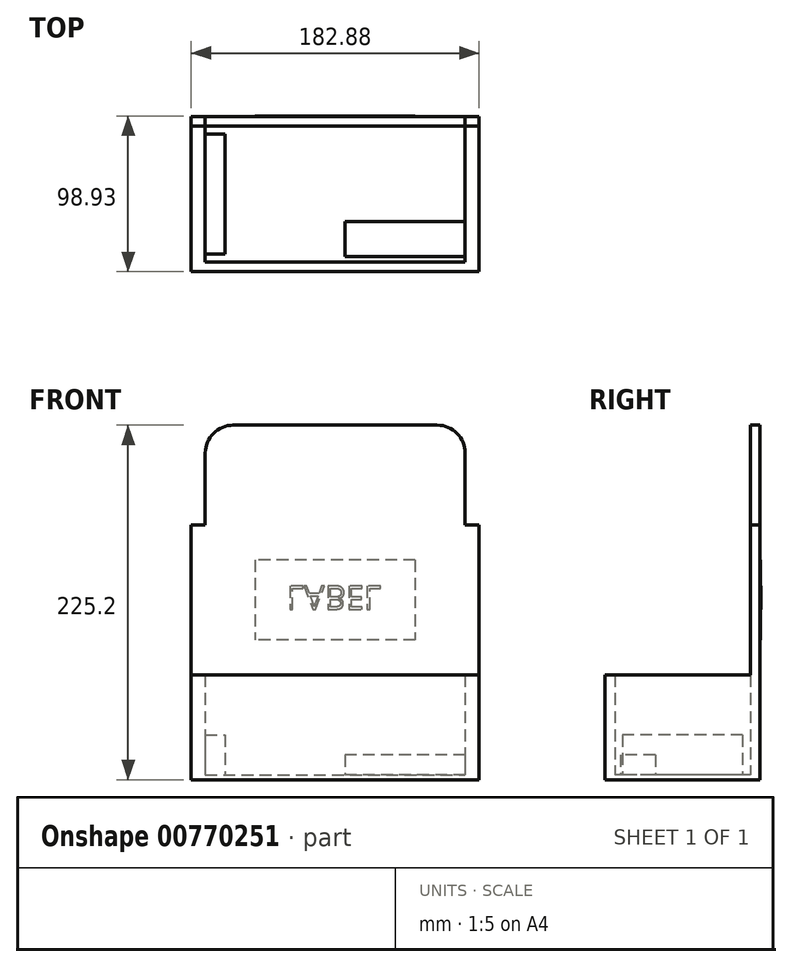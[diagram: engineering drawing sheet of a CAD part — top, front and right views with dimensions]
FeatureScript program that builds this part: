
annotation { "Feature Type Name" : "Feature", "Feature Type Description" : "" }
export const myFeature = defineFeature(function(context is Context, id is Id, definition is map)
    precondition{}
    {
        {
            var Q0;
            Q0=qCreatedBy(makeId("Top.planeOp"),FACE);
            var sketch = newSketch(context, id + "F0", { "sketchPlane" : qUnion([Q0])});
            skLineSegment(sketch, "E0.bottom", {"start": v(91.44, 49.21) * mm, "end": v(-91.44, 49.21) * mm});
            skLineSegment(sketch, "E0.top", {"start": v(91.44, -49.21) * mm, "end": v(-91.44, -49.21) * mm});
            skLineSegment(sketch, "E0.left", {"start": v(91.44, 49.21) * mm, "end": v(91.44, -49.21) * mm});
            skLineSegment(sketch, "E0.right", {"start": v(-91.44, 49.21) * mm, "end": v(-91.44, -49.21) * mm});
            skPoint(sketch, "E0.middle", {"position": v(0, 0) * mm});
            skSolve(sketch);
        }
        {
            var Q0;
            Q0=makeQuery(id+"F0.imprint","IMPRINT",FACE,{"disambiguationData":[TD([[makeQuery(id+"F0.imprint","IMPRINT",EDGE,{"derivedFrom":sQuery(id+"F0.wireOp",EDGE,"E0.bottom")}),1.0]])]});
            extrude(context, id + "F1", {"entities" : qUnion([Q0]), "depth" : 2.95 * mm});
        }
        {
            var Q0;
            Q0=makeQuery(id+"F1.opExtrude","CAP_FACE",FACE,{"disambiguationData":[OSD([sQuery(id+"F0.wireOp",EDGE,"E0.bottom"),sQuery(id+"F0.wireOp",EDGE,"E0.top"),sQuery(id+"F0.wireOp",EDGE,"E0.left"),sQuery(id+"F0.wireOp",EDGE,"E0.right")])],"isStart":false});
            var sketch = newSketch(context, id + "F2", { "sketchPlane" : qUnion([Q0])});
            skLineSegment(sketch, "E1.bottom", {"start": v(-91.44, 49.21) * mm, "end": v(-82.55, 49.21) * mm});
            skLineSegment(sketch, "E1.top", {"start": v(-91.44, -49.21) * mm, "end": v(-82.55, -49.21) * mm});
            skLineSegment(sketch, "E1.left", {"start": v(-91.44, 49.21) * mm, "end": v(-91.44, -49.21) * mm});
            skLineSegment(sketch, "E1.right", {"start": v(-82.55, 49.21) * mm, "end": v(-82.55, -49.21) * mm});
            skLineSegment(sketch, "E2.MirrorCS", {"start": v(82.55, 49.21) * mm, "end": v(82.55, -49.21) * mm});
            skLineSegment(sketch, "E3.MirrorCS", {"start": v(91.44, 49.21) * mm, "end": v(82.55, 49.21) * mm});
            skLineSegment(sketch, "E4.MirrorCS", {"start": v(91.44, -49.21) * mm, "end": v(82.55, -49.21) * mm});
            skLineSegment(sketch, "E5.MirrorCS", {"start": v(91.44, 49.21) * mm, "end": v(91.44, -49.21) * mm});
            skLineSegment(sketch, "E6", {"start": v(-82.55, -49.21) * mm, "end": v(-82.55, -43.1) * mm});
            skLineSegment(sketch, "E7", {"start": v(-82.55, -43.1) * mm, "end": v(82.55, -43.1) * mm});
            skLineSegment(sketch, "E8", {"start": v(-82.55, -49.21) * mm, "end": v(82.55, -49.21) * mm});
            skLineSegment(sketch, "E9.MirrorCS", {"start": v(-82.55, 43.1) * mm, "end": v(82.55, 43.1) * mm});
            skLineSegment(sketch, "E10.MirrorCS", {"start": v(-82.55, 49.21) * mm, "end": v(82.55, 49.21) * mm});
            skSolve(sketch);
        }
        {
            var Q0;
            Q0=qSketchRegion(id+"F2",true);
            extrude(context, id + "F3", {"entities" : qUnion([Q0]), "operationType" : NewBodyOperationType.ADD, "depth" : 63.5 * mm});
        }
        {
            var Q0;
            Q0=makeQuery(id+"F3.opExtrude","CAP_FACE",FACE,{"disambiguationData":[OSD([sQuery(id+"F2.wireOp",EDGE,"E1.bottom"),sQuery(id+"F2.wireOp",EDGE,"E1.top"),sQuery(id+"F2.wireOp",EDGE,"E1.left"),sQuery(id+"F2.wireOp",EDGE,"E1.right"),sQuery(id+"F2.wireOp",EDGE,"E2.MirrorCS"),sQuery(id+"F2.wireOp",EDGE,"E3.MirrorCS"),sQuery(id+"F2.wireOp",EDGE,"E4.MirrorCS"),sQuery(id+"F2.wireOp",EDGE,"E5.MirrorCS"),sQuery(id+"F2.wireOp",EDGE,"E7"),sQuery(id+"F2.wireOp",EDGE,"E8"),sQuery(id+"F2.wireOp",EDGE,"E9.MirrorCS"),sQuery(id+"F2.wireOp",EDGE,"E10.MirrorCS")])],"isStart":false});
            var sketch = newSketch(context, id + "F4", { "sketchPlane" : qUnion([Q0])});
            skLineSegment(sketch, "E11.bottom", {"start": v(-91.44, 49.21) * mm, "end": v(91.44, 49.21) * mm});
            skLineSegment(sketch, "E11.top", {"start": v(-91.44, 43.1) * mm, "end": v(91.44, 43.1) * mm});
            skLineSegment(sketch, "E11.left", {"start": v(-91.44, 49.21) * mm, "end": v(-91.44, 43.1) * mm});
            skLineSegment(sketch, "E11.right", {"start": v(91.44, 49.21) * mm, "end": v(91.44, 43.1) * mm});
            skSolve(sketch);
        }
        {
            var Q0;
            Q0=qSketchRegion(id+"F4",true);
            extrude(context, id + "F5", {"entities" : qUnion([Q0]), "operationType" : NewBodyOperationType.ADD, "depth" : 95.25 * mm});
        }
        {
            var Q0;
            Q0=makeQuery(id+"F5.opExtrude","CAP_FACE",FACE,{"disambiguationData":[OSD([sQuery(id+"F4.wireOp",EDGE,"E11.bottom"),sQuery(id+"F4.wireOp",EDGE,"E11.top"),sQuery(id+"F4.wireOp",EDGE,"E11.left"),sQuery(id+"F4.wireOp",EDGE,"E11.right")])],"isStart":false});
            var sketch = newSketch(context, id + "F6", { "sketchPlane" : qUnion([Q0])});
            skLineSegment(sketch, "E12.bottom", {"start": v(-82.55, 49.21) * mm, "end": v(82.55, 49.21) * mm});
            skLineSegment(sketch, "E12.top", {"start": v(-82.55, 43.1) * mm, "end": v(82.55, 43.1) * mm});
            skLineSegment(sketch, "E12.left", {"start": v(-82.55, 49.21) * mm, "end": v(-82.55, 43.1) * mm});
            skLineSegment(sketch, "E12.right", {"start": v(82.55, 49.21) * mm, "end": v(82.55, 43.1) * mm});
            skSolve(sketch);
        }
        {
            var Q0;
            Q0=qSketchRegion(id+"F6",true);
            extrude(context, id + "F7", {"entities" : qUnion([Q0]), "operationType" : NewBodyOperationType.ADD, "depth" : 63.5 * mm});
        }
        {
            var Q0;
            Q0=makeQuery(id+"F7.opExtrude","CAP_EDGE",EDGE,{"disambiguationData":[OSD([sQuery(id+"F6.wireOp",EDGE,"E12.left")])],"isStart":false});
            var Q1;
            Q1=makeQuery(id+"F7.opExtrude","CAP_EDGE",EDGE,{"disambiguationData":[OSD([sQuery(id+"F6.wireOp",EDGE,"E12.right")])],"isStart":false});
            fillet(context, id + "F8", {"entities" : qUnion([Q0, Q1]), "radius" : 17.78 * mm, "tangentPropagation" : true, "allowEdgeOverflow" : false});
        }
        {
            var Q0;
            Q0=makeQuery(id+"F7.boolean.opBoolean","MERGE",FACE,{"derivedFrom":[makeQuery(id+"F5.boolean.opBoolean","MERGE",FACE,{"derivedFrom":[makeQuery(id+"F3.boolean.opBoolean","MERGE",FACE,{"derivedFrom":[makeQuery(id+"F1.opExtrude","SWEPT_FACE",FACE,{"disambiguationData":[OSD([sQuery(id+"F0.wireOp",EDGE,"E0.bottom")])]}),makeQuery(id+"F3.opExtrude","SWEPT_FACE",FACE,{"disambiguationData":[OSD([sQuery(id+"F2.wireOp",EDGE,"E1.bottom"),sQuery(id+"F2.wireOp",EDGE,"E3.MirrorCS"),sQuery(id+"F2.wireOp",EDGE,"E10.MirrorCS")])]})]}),makeQuery(id+"F5.opExtrude","SWEPT_FACE",FACE,{"disambiguationData":[OSD([sQuery(id+"F4.wireOp",EDGE,"E11.bottom")])]})]}),makeQuery(id+"F7.opExtrude","SWEPT_FACE",FACE,{"disambiguationData":[OSD([sQuery(id+"F6.wireOp",EDGE,"E12.bottom")])]})]});
            var sketch = newSketch(context, id + "F9", { "sketchPlane" : qUnion([Q0])});
            skLineSegment(sketch, "E13.bottom", {"start": v(-50.8, 139.47) * mm, "end": v(50.8, 139.47) * mm});
            skLineSegment(sketch, "E13.top", {"start": v(-50.8, 88.67) * mm, "end": v(50.8, 88.67) * mm});
            skLineSegment(sketch, "E13.left", {"start": v(-50.8, 139.47) * mm, "end": v(-50.8, 88.67) * mm});
            skLineSegment(sketch, "E13.right", {"start": v(50.8, 139.47) * mm, "end": v(50.8, 88.67) * mm});
            skSolve(sketch);
        }
        {
            var Q0;
            Q0=qSketchRegion(id+"F9",true);
            extrude(context, id + "F10", {"entities" : qUnion([Q0]), "operationType" : NewBodyOperationType.ADD, "depth" : 0.25 * mm});
        }
        {
            var Q0;
            Q0=makeQuery(id+"F1.opExtrude","CAP_FACE",FACE,{"disambiguationData":[OSD([sQuery(id+"F0.wireOp",EDGE,"E0.bottom"),sQuery(id+"F0.wireOp",EDGE,"E0.top"),sQuery(id+"F0.wireOp",EDGE,"E0.left"),sQuery(id+"F0.wireOp",EDGE,"E0.right")])],"isStart":false});
            var sketch = newSketch(context, id + "F11", { "sketchPlane" : qUnion([Q0])});
            skLineSegment(sketch, "E14.bottom", {"start": v(-82.55, 38.1) * mm, "end": v(-69.85, 38.1) * mm});
            skLineSegment(sketch, "E14.top", {"start": v(-82.55, -38.1) * mm, "end": v(-69.85, -38.1) * mm});
            skLineSegment(sketch, "E14.left", {"start": v(-82.55, 38.1) * mm, "end": v(-82.55, -38.1) * mm});
            skLineSegment(sketch, "E14.right", {"start": v(-69.85, 38.1) * mm, "end": v(-69.85, -38.1) * mm});
            skSolve(sketch);
        }
        {
            var Q0;
            Q0=qSketchRegion(id+"F11",true);
            extrude(context, id + "F12", {"entities" : qUnion([Q0]), "operationType" : NewBodyOperationType.ADD, "depth" : 25.4 * mm});
        }
        {
            var Q0;
            Q0=makeQuery(id+"F1.opExtrude","CAP_FACE",FACE,{"disambiguationData":[OSD([sQuery(id+"F0.wireOp",EDGE,"E0.bottom"),sQuery(id+"F0.wireOp",EDGE,"E0.top"),sQuery(id+"F0.wireOp",EDGE,"E0.left"),sQuery(id+"F0.wireOp",EDGE,"E0.right")])],"isStart":false});
            var sketch = newSketch(context, id + "F13", { "sketchPlane" : qUnion([Q0])});
            skLineSegment(sketch, "E15.top", {"start": v(82.55, -17.38) * mm, "end": v(6.35, -17.38) * mm});
            skLineSegment(sketch, "E16", {"start": v(6.35, -17.38) * mm, "end": v(6.35, -39.6) * mm});
            skLineSegment(sketch, "E17", {"start": v(82.55, -17.38) * mm, "end": v(82.55, -39.6) * mm});
            skLineSegment(sketch, "E18", {"start": v(82.55, -39.6) * mm, "end": v(6.35, -39.6) * mm});
            skSolve(sketch);
        }
        {
            var Q0;
            Q0=qSketchRegion(id+"F13",true);
            extrude(context, id + "F14", {"entities" : qUnion([Q0]), "operationType" : NewBodyOperationType.ADD, "depth" : 12.7 * mm});
        }
        {
            var Q0;
            Q0=makeQuery(id+"F10.opExtrude","CAP_FACE",FACE,{"disambiguationData":[OSD([sQuery(id+"F9.wireOp",EDGE,"E13.bottom"),sQuery(id+"F9.wireOp",EDGE,"E13.top"),sQuery(id+"F9.wireOp",EDGE,"E13.left"),sQuery(id+"F9.wireOp",EDGE,"E13.right")])],"isStart":false});
            var sketch = newSketch(context, id + "F15", { "sketchPlane" : qUnion([Q0])});
            skText(sketch, "E19", { "text": "LABEL", "fontName": "OpenSans-Regular.ttf"});
            const initialGuessF15  = {"E19": [0.03075, 0.12303, -1, 0, 0.01498]};
            skSetInitialGuess(sketch, initialGuessF15);
            skSolve(sketch);
        }
        {
            var Q0;
            Q0=qSketchRegion(id+"F15",true);
            extrude(context, id + "F16", {"entities" : qUnion([Q0]), "operationType" : NewBodyOperationType.ADD, "depth" : 0.25 * mm});
        }
    });
